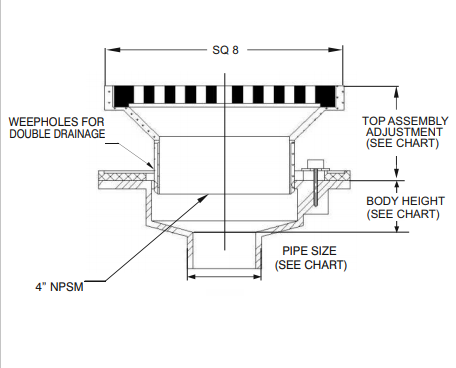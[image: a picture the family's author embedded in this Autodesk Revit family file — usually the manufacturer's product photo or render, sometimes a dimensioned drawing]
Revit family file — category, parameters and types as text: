
# Revit family: R1200-PR
name_source: partatom
category: Plumbing Fixtures
revit_build: Autodesk Revit 2018 (Build: 20170223_1515(x64)
units: mm (PartAtom-declared; Revit-internal decimal feet)

## family parameters
Cut with Voids When Loaded = No
Host = Face
Part Type = Normal
Room Calculation Point = No
Round Connector Dimension = Use Radius
Shared = No

## types (6) — shared parameters
Default Elevation = 0' - 0"
Description = LARGE SUMP PROMENADE DECK DRAIN WITH 12 3/4" x 12 3/4" TOP
Floor Drain Material = Paint - Sherwin Williams Paint - #952C2A - Bellwood Red
Manufacturer = MIFAB
Top Assembly Adjustment = 0' - 2 1/2"
URL = WWW.MIFAB.COM
zero-valued in all types: CWFU, WFU

## per-type parameters (varying)
| type | Model | Pipe Diameter | Pipe Radius |
| R1205, 6-PR_6" Drain Pipe Size | R1205, 6-PR | 0' - 6" | 0' - 3" |
| R1208-PR_8" Drain Pipe Size | R1208-PR | 0' - 8" | 0' - 4" |
| R1205, 6-PR_5" Drain Pipe Size | R1205, 6-PR | 0' - 5" | 0' - 2 1/2" |
| R1202, 3, 4-PR_4" Drain Pipe Size | R1202, 3, 4-PR | 0' - 4" | 0' - 2" |
| R1202, 3, 4-PR_3" Drain Pipe Size | R1202, 3, 4-PR | 0' - 3" | 0' - 1 1/2" |
| R1202, 3, 4-PR_2" Drain Pipe Size | R1202, 3, 4-PR | 0' - 2" | 0' - 1" |

## geometry (parser evidence)
native form markers: Blend x2, Sweep x6
no freeform markers — native parametric forms only
